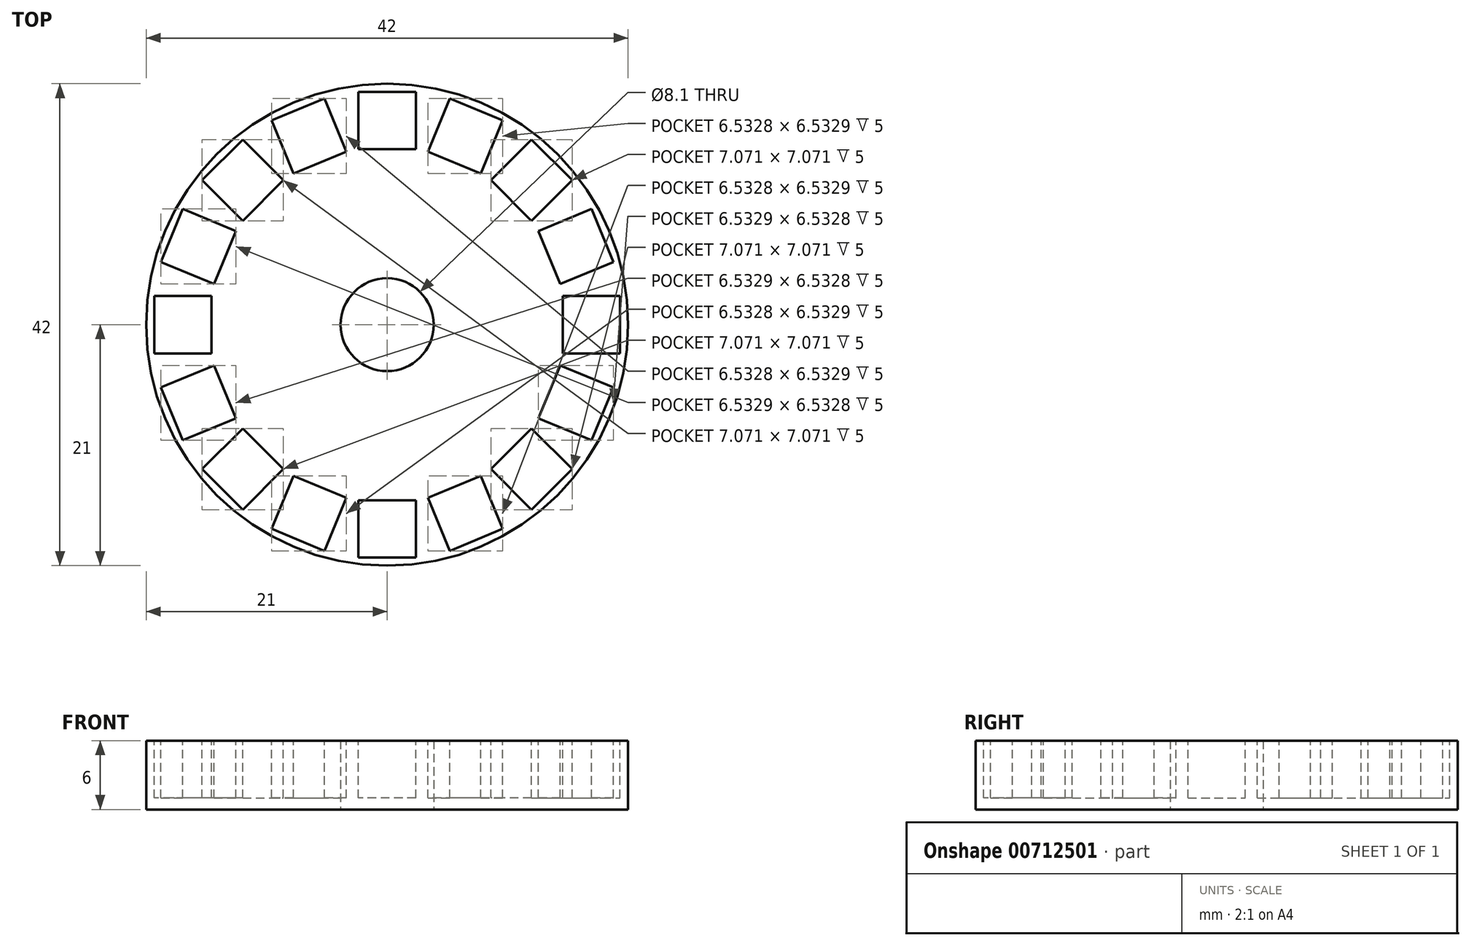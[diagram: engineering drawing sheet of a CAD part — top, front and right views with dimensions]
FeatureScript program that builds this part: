
annotation { "Feature Type Name" : "Feature", "Feature Type Description" : "" }
export const myFeature = defineFeature(function(context is Context, id is Id, definition is map)
    precondition{}
    {
        {
            var Q0;
            Q0=qCreatedBy(makeId("Front.planeOp"),FACE);
            var sketch = newSketch(context, id + "F0", { "sketchPlane" : qUnion([Q0])});
            skLineSegment(sketch, "E0", {"start": v(0, 0) * mm, "end": v(21, 0) * mm});
            skLineSegment(sketch, "E1", {"start": v(21, 0) * mm, "end": v(21, 6) * mm});
            skLineSegment(sketch, "E2", {"start": v(21, 6) * mm, "end": v(0, 6) * mm});
            skLineSegment(sketch, "E3", {"start": v(0, 6) * mm, "end": v(0, 0) * mm});
            skSolve(sketch);
        }
        {
            var Q0;
            Q0 = qSketchRegion(id + "F0", true);
            var Q1;
            Q1=sQuery(id+"F0.wireOp",EDGE,"E3");
            revolve(context, id + "F1", {"surfaceOperationType" : NewSurfaceOperationType.NEW, "entities" : qUnion([Q0]), "axis" : qUnion([Q1]), "revolveType" : RevolveType.FULL});
        }
        {
            var Q0;
            Q0=qCreatedBy(makeId("Top.planeOp"),FACE);
            var sketch = newSketch(context, id + "F2", { "sketchPlane" : qUnion([Q0])});
            skCircle(sketch, "E4", {"center": v(0, 0) * mm, "radius": 8.9 * mm});
            skCircle(sketch, "E5", {"center": v(0, 0) * mm, "radius": 12.96 * mm});
            skCircle(sketch, "E6", {"center": v(0, 0) * mm, "radius": 17.01 * mm});
            skCircle(sketch, "E7", {"center": v(0, 0) * mm, "radius": 4.05 * mm});
            skSolve(sketch);
        }
        {
            var Q0;
            Q0=makeQuery(id+"F2.imprint","IMPRINT",FACE,{"disambiguationData":[TD([[makeQuery(id+"F2.imprint","IMPRINT",EDGE,{"derivedFrom":sQuery(id+"F2.wireOp",EDGE,"E7")}),1.0]])]});
            extrude(context, id + "F3", {"entities" : qUnion([Q0]), "operationType" : NewBodyOperationType.REMOVE, "depth" : 25 * mm, "offsetDistance" : 25 * mm});
        }
        {
            var Q0;
            Q0=makeQuery(id+"F1.opRevolve","SWEPT_FACE",FACE,{"disambiguationData":[OSD([sQuery(id+"F0.wireOp",EDGE,"E2")])]});
            var sketch = newSketch(context, id + "F4", { "sketchPlane" : qUnion([Q0])});
            skLineSegment(sketch, "E8.bottom", {"start": v(2.5, 15.3) * mm, "end": v(-2.5, 15.3) * mm});
            skLineSegment(sketch, "E8.top", {"start": v(2.5, 20.3) * mm, "end": v(-2.5, 20.3) * mm});
            skLineSegment(sketch, "E8.left", {"start": v(2.5, 15.3) * mm, "end": v(2.5, 20.3) * mm});
            skLineSegment(sketch, "E8.right", {"start": v(-2.5, 15.3) * mm, "end": v(-2.5, 20.3) * mm});
            skLineSegment(sketch, "E9", {"start": v(0, 0) * mm, "end": v(0, 15.3) * mm, "construction": true});
            skLineSegment(sketch, "E10.1.0", {"start": v(-3.55, 15.1) * mm, "end": v(-5.46, 19.71) * mm});
            skLineSegment(sketch, "E10.1.1", {"start": v(-5.46, 19.71) * mm, "end": v(-10.08, 17.8) * mm});
            skLineSegment(sketch, "E10.1.2", {"start": v(-8.16, 13.18) * mm, "end": v(-10.08, 17.8) * mm});
            skLineSegment(sketch, "E10.1.3", {"start": v(-3.55, 15.1) * mm, "end": v(-8.16, 13.18) * mm});
            skLineSegment(sketch, "E10.2.0", {"start": v(-9.05, 12.59) * mm, "end": v(-12.59, 16.12) * mm});
            skLineSegment(sketch, "E10.2.1", {"start": v(-12.59, 16.12) * mm, "end": v(-16.12, 12.59) * mm});
            skLineSegment(sketch, "E10.2.2", {"start": v(-12.59, 9.05) * mm, "end": v(-16.12, 12.59) * mm});
            skLineSegment(sketch, "E10.2.3", {"start": v(-9.05, 12.59) * mm, "end": v(-12.59, 9.05) * mm});
            skLineSegment(sketch, "E10.3.0", {"start": v(-13.18, 8.16) * mm, "end": v(-17.8, 10.08) * mm});
            skLineSegment(sketch, "E10.3.1", {"start": v(-17.8, 10.08) * mm, "end": v(-19.71, 5.46) * mm});
            skLineSegment(sketch, "E10.3.2", {"start": v(-15.1, 3.55) * mm, "end": v(-19.71, 5.46) * mm});
            skLineSegment(sketch, "E10.3.3", {"start": v(-13.18, 8.16) * mm, "end": v(-15.1, 3.55) * mm});
            skLineSegment(sketch, "E10.4.0", {"start": v(-15.3, 2.5) * mm, "end": v(-20.3, 2.5) * mm});
            skLineSegment(sketch, "E10.4.1", {"start": v(-20.3, 2.5) * mm, "end": v(-20.3, -2.5) * mm});
            skLineSegment(sketch, "E10.4.2", {"start": v(-15.3, -2.5) * mm, "end": v(-20.3, -2.5) * mm});
            skLineSegment(sketch, "E10.4.3", {"start": v(-15.3, 2.5) * mm, "end": v(-15.3, -2.5) * mm});
            skLineSegment(sketch, "E10.5.0", {"start": v(-15.1, -3.55) * mm, "end": v(-19.71, -5.46) * mm});
            skLineSegment(sketch, "E10.5.1", {"start": v(-19.71, -5.46) * mm, "end": v(-17.8, -10.08) * mm});
            skLineSegment(sketch, "E10.5.2", {"start": v(-13.18, -8.16) * mm, "end": v(-17.8, -10.08) * mm});
            skLineSegment(sketch, "E10.5.3", {"start": v(-15.1, -3.55) * mm, "end": v(-13.18, -8.16) * mm});
            skLineSegment(sketch, "E10.6.0", {"start": v(-12.59, -9.05) * mm, "end": v(-16.12, -12.59) * mm});
            skLineSegment(sketch, "E10.6.1", {"start": v(-16.12, -12.59) * mm, "end": v(-12.59, -16.12) * mm});
            skLineSegment(sketch, "E10.6.2", {"start": v(-9.05, -12.59) * mm, "end": v(-12.59, -16.12) * mm});
            skLineSegment(sketch, "E10.6.3", {"start": v(-12.59, -9.05) * mm, "end": v(-9.05, -12.59) * mm});
            skLineSegment(sketch, "E10.7.0", {"start": v(-8.16, -13.18) * mm, "end": v(-10.08, -17.8) * mm});
            skLineSegment(sketch, "E10.7.1", {"start": v(-10.08, -17.8) * mm, "end": v(-5.46, -19.71) * mm});
            skLineSegment(sketch, "E10.7.2", {"start": v(-3.55, -15.1) * mm, "end": v(-5.46, -19.71) * mm});
            skLineSegment(sketch, "E10.7.3", {"start": v(-8.16, -13.18) * mm, "end": v(-3.55, -15.1) * mm});
            skLineSegment(sketch, "E10.8.0", {"start": v(-2.5, -15.3) * mm, "end": v(-2.5, -20.3) * mm});
            skLineSegment(sketch, "E10.8.1", {"start": v(-2.5, -20.3) * mm, "end": v(2.5, -20.3) * mm});
            skLineSegment(sketch, "E10.8.2", {"start": v(2.5, -15.3) * mm, "end": v(2.5, -20.3) * mm});
            skLineSegment(sketch, "E10.8.3", {"start": v(-2.5, -15.3) * mm, "end": v(2.5, -15.3) * mm});
            skLineSegment(sketch, "E10.9.0", {"start": v(3.55, -15.1) * mm, "end": v(5.46, -19.71) * mm});
            skLineSegment(sketch, "E10.9.1", {"start": v(5.46, -19.71) * mm, "end": v(10.08, -17.8) * mm});
            skLineSegment(sketch, "E10.9.2", {"start": v(8.16, -13.18) * mm, "end": v(10.08, -17.8) * mm});
            skLineSegment(sketch, "E10.9.3", {"start": v(3.55, -15.1) * mm, "end": v(8.16, -13.18) * mm});
            skLineSegment(sketch, "E10.10.0", {"start": v(9.05, -12.59) * mm, "end": v(12.59, -16.12) * mm});
            skLineSegment(sketch, "E10.10.1", {"start": v(12.59, -16.12) * mm, "end": v(16.12, -12.59) * mm});
            skLineSegment(sketch, "E10.10.2", {"start": v(12.59, -9.05) * mm, "end": v(16.12, -12.59) * mm});
            skLineSegment(sketch, "E10.10.3", {"start": v(9.05, -12.59) * mm, "end": v(12.59, -9.05) * mm});
            skLineSegment(sketch, "E10.11.0", {"start": v(13.18, -8.16) * mm, "end": v(17.8, -10.08) * mm});
            skLineSegment(sketch, "E10.11.1", {"start": v(17.8, -10.08) * mm, "end": v(19.71, -5.46) * mm});
            skLineSegment(sketch, "E10.11.2", {"start": v(15.1, -3.55) * mm, "end": v(19.71, -5.46) * mm});
            skLineSegment(sketch, "E10.11.3", {"start": v(13.18, -8.16) * mm, "end": v(15.1, -3.55) * mm});
            skLineSegment(sketch, "E10.12.0", {"start": v(15.3, -2.5) * mm, "end": v(20.3, -2.5) * mm});
            skLineSegment(sketch, "E10.12.1", {"start": v(20.3, -2.5) * mm, "end": v(20.3, 2.5) * mm});
            skLineSegment(sketch, "E10.12.2", {"start": v(15.3, 2.5) * mm, "end": v(20.3, 2.5) * mm});
            skLineSegment(sketch, "E10.12.3", {"start": v(15.3, -2.5) * mm, "end": v(15.3, 2.5) * mm});
            skLineSegment(sketch, "E10.13.0", {"start": v(15.1, 3.55) * mm, "end": v(19.71, 5.46) * mm});
            skLineSegment(sketch, "E10.13.1", {"start": v(19.71, 5.46) * mm, "end": v(17.8, 10.08) * mm});
            skLineSegment(sketch, "E10.13.2", {"start": v(13.18, 8.16) * mm, "end": v(17.8, 10.08) * mm});
            skLineSegment(sketch, "E10.13.3", {"start": v(15.1, 3.55) * mm, "end": v(13.18, 8.16) * mm});
            skLineSegment(sketch, "E10.14.0", {"start": v(12.59, 9.05) * mm, "end": v(16.12, 12.59) * mm});
            skLineSegment(sketch, "E10.14.1", {"start": v(16.12, 12.59) * mm, "end": v(12.59, 16.12) * mm});
            skLineSegment(sketch, "E10.14.2", {"start": v(9.05, 12.59) * mm, "end": v(12.59, 16.12) * mm});
            skLineSegment(sketch, "E10.14.3", {"start": v(12.59, 9.05) * mm, "end": v(9.05, 12.59) * mm});
            skLineSegment(sketch, "E10.15.0", {"start": v(8.16, 13.18) * mm, "end": v(10.08, 17.8) * mm});
            skLineSegment(sketch, "E10.15.1", {"start": v(10.08, 17.8) * mm, "end": v(5.46, 19.71) * mm});
            skLineSegment(sketch, "E10.15.2", {"start": v(3.55, 15.1) * mm, "end": v(5.46, 19.71) * mm});
            skLineSegment(sketch, "E10.15.3", {"start": v(8.16, 13.18) * mm, "end": v(3.55, 15.1) * mm});
            skPoint(sketch, "E10.center", {"position": v(0, 0) * mm});
            skSolve(sketch);
        }
        {
            var Q0;
            {var subQ0=sQuery(id+"F4.wireOp",EDGE,"6b0e4d02-cffa-4799-8ca5-8f1609af44a9.1.3");Q0=makeQuery(id+"F4.imprint","IMPRINT",FACE,{"disambiguationData":[TD([[makeQuery(id+"F4.imprint","IMPRINT",EDGE,{"derivedFrom":subQ0}),-1.0]])]});}
            var Q1;
            {var subQ0=sQuery(id+"F4.wireOp",EDGE,"E8.bottom");Q1=makeQuery(id+"F4.imprint","IMPRINT",FACE,{"disambiguationData":[TD([[makeQuery(id+"F4.imprint","IMPRINT",EDGE,{"derivedFrom":subQ0}),-1.0]])]});}
            var Q2;
            {var subQ0=sQuery(id+"F4.wireOp",EDGE,"90cd43ab-74c5-4661-9c80-5ee8405ae9ff.9.15.0");Q2=makeQuery(id+"F4.imprint","IMPRINT",FACE,{"disambiguationData":[TD([[makeQuery(id+"F4.imprint","IMPRINT",EDGE,{"derivedFrom":subQ0}),-1.0]])]});}
            var Q3;
            {var subQ0=sQuery(id+"F4.wireOp",EDGE,"90cd43ab-74c5-4661-9c80-5ee8405ae9ff.9.14.0");Q3=makeQuery(id+"F4.imprint","IMPRINT",FACE,{"disambiguationData":[TD([[makeQuery(id+"F4.imprint","IMPRINT",EDGE,{"derivedFrom":subQ0}),-1.0]])]});}
            var Q4;
            {var subQ0=sQuery(id+"F4.wireOp",EDGE,"90cd43ab-74c5-4661-9c80-5ee8405ae9ff.9.13.0");Q4=makeQuery(id+"F4.imprint","IMPRINT",FACE,{"disambiguationData":[TD([[makeQuery(id+"F4.imprint","IMPRINT",EDGE,{"derivedFrom":subQ0}),-1.0]])]});}
            var Q5;
            {var subQ0=sQuery(id+"F4.wireOp",EDGE,"90cd43ab-74c5-4661-9c80-5ee8405ae9ff.9.12.0");Q5=makeQuery(id+"F4.imprint","IMPRINT",FACE,{"disambiguationData":[TD([[makeQuery(id+"F4.imprint","IMPRINT",EDGE,{"derivedFrom":subQ0}),-1.0]])]});}
            var Q6;
            {var subQ0=sQuery(id+"F4.wireOp",EDGE,"90cd43ab-74c5-4661-9c80-5ee8405ae9ff.9.11.0");Q6=makeQuery(id+"F4.imprint","IMPRINT",FACE,{"disambiguationData":[TD([[makeQuery(id+"F4.imprint","IMPRINT",EDGE,{"derivedFrom":subQ0}),-1.0]])]});}
            var Q7;
            {var subQ0=sQuery(id+"F4.wireOp",EDGE,"90cd43ab-74c5-4661-9c80-5ee8405ae9ff.9.10.0");Q7=makeQuery(id+"F4.imprint","IMPRINT",FACE,{"disambiguationData":[TD([[makeQuery(id+"F4.imprint","IMPRINT",EDGE,{"derivedFrom":subQ0}),-1.0]])]});}
            var Q8;
            {var subQ0=sQuery(id+"F4.wireOp",EDGE,"90cd43ab-74c5-4661-9c80-5ee8405ae9ff.9.9.0");Q8=makeQuery(id+"F4.imprint","IMPRINT",FACE,{"disambiguationData":[TD([[makeQuery(id+"F4.imprint","IMPRINT",EDGE,{"derivedFrom":subQ0}),-1.0]])]});}
            var Q9;
            {var subQ0=sQuery(id+"F4.wireOp",EDGE,"90cd43ab-74c5-4661-9c80-5ee8405ae9ff.9.8.0");Q9=makeQuery(id+"F4.imprint","IMPRINT",FACE,{"disambiguationData":[TD([[makeQuery(id+"F4.imprint","IMPRINT",EDGE,{"derivedFrom":subQ0}),-1.0]])]});}
            var Q10;
            {var subQ0=sQuery(id+"F4.wireOp",EDGE,"90cd43ab-74c5-4661-9c80-5ee8405ae9ff.9.7.0");Q10=makeQuery(id+"F4.imprint","IMPRINT",FACE,{"disambiguationData":[TD([[makeQuery(id+"F4.imprint","IMPRINT",EDGE,{"derivedFrom":subQ0}),-1.0]])]});}
            var Q11;
            {var subQ0=sQuery(id+"F4.wireOp",EDGE,"90cd43ab-74c5-4661-9c80-5ee8405ae9ff.9.6.0");Q11=makeQuery(id+"F4.imprint","IMPRINT",FACE,{"disambiguationData":[TD([[makeQuery(id+"F4.imprint","IMPRINT",EDGE,{"derivedFrom":subQ0}),-1.0]])]});}
            var Q12;
            {var subQ0=sQuery(id+"F4.wireOp",EDGE,"90cd43ab-74c5-4661-9c80-5ee8405ae9ff.9.5.0");Q12=makeQuery(id+"F4.imprint","IMPRINT",FACE,{"disambiguationData":[TD([[makeQuery(id+"F4.imprint","IMPRINT",EDGE,{"derivedFrom":subQ0}),-1.0]])]});}
            var Q13;
            {var subQ0=sQuery(id+"F4.wireOp",EDGE,"90cd43ab-74c5-4661-9c80-5ee8405ae9ff.9.4.0");Q13=makeQuery(id+"F4.imprint","IMPRINT",FACE,{"disambiguationData":[TD([[makeQuery(id+"F4.imprint","IMPRINT",EDGE,{"derivedFrom":subQ0}),-1.0]])]});}
            var Q14;
            {var subQ0=sQuery(id+"F4.wireOp",EDGE,"90cd43ab-74c5-4661-9c80-5ee8405ae9ff.9.3.0");Q14=makeQuery(id+"F4.imprint","IMPRINT",FACE,{"disambiguationData":[TD([[makeQuery(id+"F4.imprint","IMPRINT",EDGE,{"derivedFrom":subQ0}),-1.0]])]});}
            var Q15;
            {var subQ0=sQuery(id+"F4.wireOp",EDGE,"6b0e4d02-cffa-4799-8ca5-8f1609af44a9.2.3");Q15=makeQuery(id+"F4.imprint","IMPRINT",FACE,{"disambiguationData":[TD([[makeQuery(id+"F4.imprint","IMPRINT",EDGE,{"derivedFrom":subQ0}),-1.0]])]});}
            var Q16;
            Q16=makeQuery(id+"F4.imprint","IMPRINT",FACE,{"disambiguationData":[TD([[makeQuery(id+"F4.imprint","IMPRINT",EDGE,{"derivedFrom":sQuery(id+"F4.wireOp",EDGE,"d7aad85c-847f-47a7-b33a-bcce6dfe605d.15.0")}),-1.0]])]});
            var Q17;
            Q17=makeQuery(id+"F4.imprint","IMPRINT",FACE,{"disambiguationData":[TD([[makeQuery(id+"F4.imprint","IMPRINT",EDGE,{"derivedFrom":sQuery(id+"F4.wireOp",EDGE,"d7aad85c-847f-47a7-b33a-bcce6dfe605d.14.0")}),-1.0]])]});
            var Q18;
            Q18=makeQuery(id+"F4.imprint","IMPRINT",FACE,{"disambiguationData":[TD([[makeQuery(id+"F4.imprint","IMPRINT",EDGE,{"derivedFrom":sQuery(id+"F4.wireOp",EDGE,"d7aad85c-847f-47a7-b33a-bcce6dfe605d.13.0")}),-1.0]])]});
            var Q19;
            Q19=makeQuery(id+"F4.imprint","IMPRINT",FACE,{"disambiguationData":[TD([[makeQuery(id+"F4.imprint","IMPRINT",EDGE,{"derivedFrom":sQuery(id+"F4.wireOp",EDGE,"d7aad85c-847f-47a7-b33a-bcce6dfe605d.12.0")}),-1.0]])]});
            var Q20;
            Q20=makeQuery(id+"F4.imprint","IMPRINT",FACE,{"disambiguationData":[TD([[makeQuery(id+"F4.imprint","IMPRINT",EDGE,{"derivedFrom":sQuery(id+"F4.wireOp",EDGE,"d7aad85c-847f-47a7-b33a-bcce6dfe605d.11.0")}),-1.0]])]});
            var Q21;
            Q21=makeQuery(id+"F4.imprint","IMPRINT",FACE,{"disambiguationData":[TD([[makeQuery(id+"F4.imprint","IMPRINT",EDGE,{"derivedFrom":sQuery(id+"F4.wireOp",EDGE,"d7aad85c-847f-47a7-b33a-bcce6dfe605d.10.0")}),-1.0]])]});
            var Q22;
            Q22=makeQuery(id+"F4.imprint","IMPRINT",FACE,{"disambiguationData":[TD([[makeQuery(id+"F4.imprint","IMPRINT",EDGE,{"derivedFrom":sQuery(id+"F4.wireOp",EDGE,"d7aad85c-847f-47a7-b33a-bcce6dfe605d.9.0")}),-1.0]])]});
            var Q23;
            Q23=makeQuery(id+"F4.imprint","IMPRINT",FACE,{"disambiguationData":[TD([[makeQuery(id+"F4.imprint","IMPRINT",EDGE,{"derivedFrom":sQuery(id+"F4.wireOp",EDGE,"d7aad85c-847f-47a7-b33a-bcce6dfe605d.8.0")}),-1.0]])]});
            var Q24;
            Q24=makeQuery(id+"F4.imprint","IMPRINT",FACE,{"disambiguationData":[TD([[makeQuery(id+"F4.imprint","IMPRINT",EDGE,{"derivedFrom":sQuery(id+"F4.wireOp",EDGE,"d7aad85c-847f-47a7-b33a-bcce6dfe605d.7.0")}),-1.0]])]});
            var Q25;
            Q25=makeQuery(id+"F4.imprint","IMPRINT",FACE,{"disambiguationData":[TD([[makeQuery(id+"F4.imprint","IMPRINT",EDGE,{"derivedFrom":sQuery(id+"F4.wireOp",EDGE,"d7aad85c-847f-47a7-b33a-bcce6dfe605d.6.0")}),-1.0]])]});
            var Q26;
            Q26=makeQuery(id+"F4.imprint","IMPRINT",FACE,{"disambiguationData":[TD([[makeQuery(id+"F4.imprint","IMPRINT",EDGE,{"derivedFrom":sQuery(id+"F4.wireOp",EDGE,"d7aad85c-847f-47a7-b33a-bcce6dfe605d.5.0")}),-1.0]])]});
            var Q27;
            Q27=makeQuery(id+"F4.imprint","IMPRINT",FACE,{"disambiguationData":[TD([[makeQuery(id+"F4.imprint","IMPRINT",EDGE,{"derivedFrom":sQuery(id+"F4.wireOp",EDGE,"d7aad85c-847f-47a7-b33a-bcce6dfe605d.4.0")}),-1.0]])]});
            var Q28;
            Q28=makeQuery(id+"F4.imprint","IMPRINT",FACE,{"disambiguationData":[TD([[makeQuery(id+"F4.imprint","IMPRINT",EDGE,{"derivedFrom":sQuery(id+"F4.wireOp",EDGE,"d7aad85c-847f-47a7-b33a-bcce6dfe605d.3.0")}),-1.0]])]});
            var Q29;
            Q29=makeQuery(id+"F4.imprint","IMPRINT",FACE,{"disambiguationData":[TD([[makeQuery(id+"F4.imprint","IMPRINT",EDGE,{"derivedFrom":sQuery(id+"F4.wireOp",EDGE,"d7aad85c-847f-47a7-b33a-bcce6dfe605d.2.0")}),-1.0]])]});
            var Q30;
            Q30=makeQuery(id+"F4.imprint","IMPRINT",FACE,{"disambiguationData":[TD([[makeQuery(id+"F4.imprint","IMPRINT",EDGE,{"derivedFrom":sQuery(id+"F4.wireOp",EDGE,"d7aad85c-847f-47a7-b33a-bcce6dfe605d.1.0")}),-1.0]])]});
            var Q31;
            Q31=makeQuery(id+"F4.imprint","IMPRINT",FACE,{"disambiguationData":[TD([[makeQuery(id+"F4.imprint","IMPRINT",EDGE,{"derivedFrom":sQuery(id+"F4.wireOp",EDGE,"E10.15.0")}),1.0]])]});
            var Q32;
            Q32=makeQuery(id+"F4.imprint","IMPRINT",FACE,{"disambiguationData":[TD([[makeQuery(id+"F4.imprint","IMPRINT",EDGE,{"derivedFrom":sQuery(id+"F4.wireOp",EDGE,"E10.14.0")}),1.0]])]});
            var Q33;
            Q33=makeQuery(id+"F4.imprint","IMPRINT",FACE,{"disambiguationData":[TD([[makeQuery(id+"F4.imprint","IMPRINT",EDGE,{"derivedFrom":sQuery(id+"F4.wireOp",EDGE,"E10.13.0")}),1.0]])]});
            var Q34;
            Q34=makeQuery(id+"F4.imprint","IMPRINT",FACE,{"disambiguationData":[TD([[makeQuery(id+"F4.imprint","IMPRINT",EDGE,{"derivedFrom":sQuery(id+"F4.wireOp",EDGE,"E10.12.0")}),1.0]])]});
            var Q35;
            Q35=makeQuery(id+"F4.imprint","IMPRINT",FACE,{"disambiguationData":[TD([[makeQuery(id+"F4.imprint","IMPRINT",EDGE,{"derivedFrom":sQuery(id+"F4.wireOp",EDGE,"E10.11.0")}),1.0]])]});
            var Q36;
            Q36=makeQuery(id+"F4.imprint","IMPRINT",FACE,{"disambiguationData":[TD([[makeQuery(id+"F4.imprint","IMPRINT",EDGE,{"derivedFrom":sQuery(id+"F4.wireOp",EDGE,"E10.10.0")}),1.0]])]});
            var Q37;
            Q37=makeQuery(id+"F4.imprint","IMPRINT",FACE,{"disambiguationData":[TD([[makeQuery(id+"F4.imprint","IMPRINT",EDGE,{"derivedFrom":sQuery(id+"F4.wireOp",EDGE,"E10.9.0")}),1.0]])]});
            var Q38;
            Q38=makeQuery(id+"F4.imprint","IMPRINT",FACE,{"disambiguationData":[TD([[makeQuery(id+"F4.imprint","IMPRINT",EDGE,{"derivedFrom":sQuery(id+"F4.wireOp",EDGE,"E10.8.0")}),1.0]])]});
            var Q39;
            Q39=makeQuery(id+"F4.imprint","IMPRINT",FACE,{"disambiguationData":[TD([[makeQuery(id+"F4.imprint","IMPRINT",EDGE,{"derivedFrom":sQuery(id+"F4.wireOp",EDGE,"E10.7.0")}),1.0]])]});
            var Q40;
            Q40=makeQuery(id+"F4.imprint","IMPRINT",FACE,{"disambiguationData":[TD([[makeQuery(id+"F4.imprint","IMPRINT",EDGE,{"derivedFrom":sQuery(id+"F4.wireOp",EDGE,"E10.6.0")}),1.0]])]});
            var Q41;
            Q41=makeQuery(id+"F4.imprint","IMPRINT",FACE,{"disambiguationData":[TD([[makeQuery(id+"F4.imprint","IMPRINT",EDGE,{"derivedFrom":sQuery(id+"F4.wireOp",EDGE,"E10.5.0")}),1.0]])]});
            var Q42;
            Q42=makeQuery(id+"F4.imprint","IMPRINT",FACE,{"disambiguationData":[TD([[makeQuery(id+"F4.imprint","IMPRINT",EDGE,{"derivedFrom":sQuery(id+"F4.wireOp",EDGE,"E10.4.0")}),1.0]])]});
            var Q43;
            Q43=makeQuery(id+"F4.imprint","IMPRINT",FACE,{"disambiguationData":[TD([[makeQuery(id+"F4.imprint","IMPRINT",EDGE,{"derivedFrom":sQuery(id+"F4.wireOp",EDGE,"E10.3.0")}),1.0]])]});
            var Q44;
            Q44=makeQuery(id+"F4.imprint","IMPRINT",FACE,{"disambiguationData":[TD([[makeQuery(id+"F4.imprint","IMPRINT",EDGE,{"derivedFrom":sQuery(id+"F4.wireOp",EDGE,"E10.2.0")}),1.0]])]});
            var Q45;
            Q45=makeQuery(id+"F4.imprint","IMPRINT",FACE,{"disambiguationData":[TD([[makeQuery(id+"F4.imprint","IMPRINT",EDGE,{"derivedFrom":sQuery(id+"F4.wireOp",EDGE,"E10.1.0")}),1.0]])]});
            extrude(context, id + "F5", {"entities" : qUnion([Q0, Q1, Q2, Q3, Q4, Q5, Q6, Q7, Q8, Q9, Q10, Q11, Q12, Q13, Q14, Q15, Q16, Q17, Q18, Q19, Q20, Q21, Q22, Q23, Q24, Q25, Q26, Q27, Q28, Q29, Q30, Q31, Q32, Q33, Q34, Q35, Q36, Q37, Q38, Q39, Q40, Q41, Q42, Q43, Q44, Q45]), "operationType" : NewBodyOperationType.REMOVE, "oppositeDirection" : true, "depth" : 5 * mm, "offsetDistance" : 25 * mm});
        }
    });
